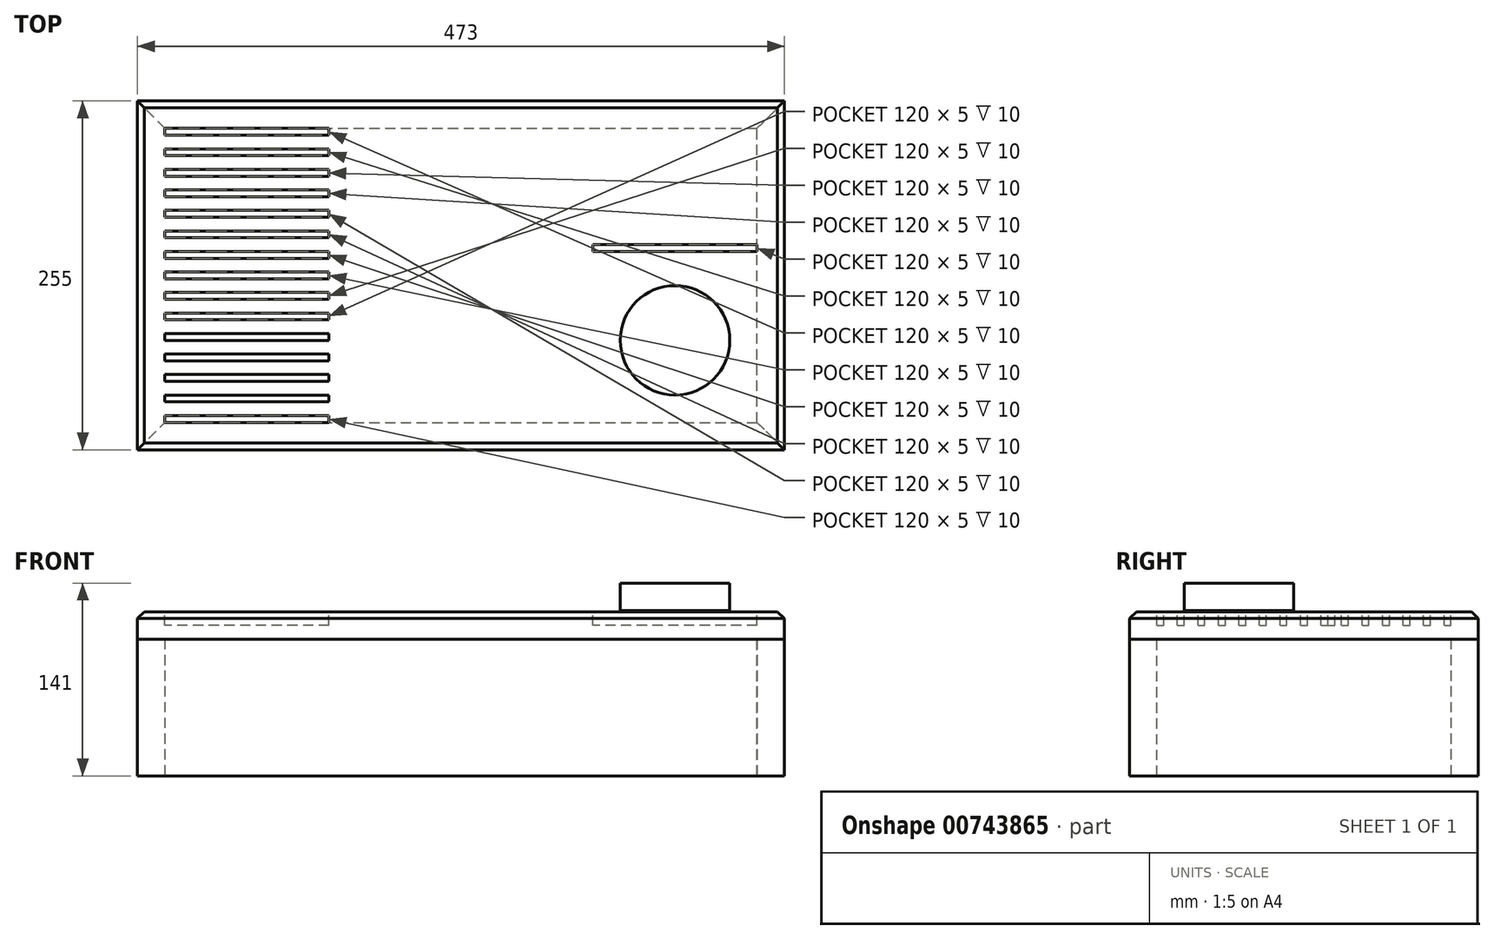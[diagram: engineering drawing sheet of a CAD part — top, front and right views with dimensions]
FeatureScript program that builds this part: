
annotation { "Feature Type Name" : "Feature", "Feature Type Description" : "" }
export const myFeature = defineFeature(function(context is Context, id is Id, definition is map)
    precondition{}
    {
        {
            var Q0;
            Q0=qCreatedBy(makeId("Top.planeOp"),FACE);
            var sketch = newSketch(context, id + "F0", { "sketchPlane" : qUnion([Q0])});
            skPoint(sketch, "E0.middle", {"position": v(0, 0) * mm});
            skLineSegment(sketch, "E1.bottom", {"start": v(-236.5, 127.5) * mm, "end": v(236.5, 127.5) * mm});
            skLineSegment(sketch, "E1.top", {"start": v(-236.5, 107.5) * mm, "end": v(236.5, 107.5) * mm});
            skLineSegment(sketch, "E1.left", {"start": v(-236.5, 127.5) * mm, "end": v(-236.5, 107.5) * mm});
            skLineSegment(sketch, "E1.right", {"start": v(236.5, 127.5) * mm, "end": v(236.5, 107.5) * mm});
            skLineSegment(sketch, "E2.bottom", {"start": v(-236.5, -127.5) * mm, "end": v(236.5, -127.5) * mm});
            skLineSegment(sketch, "E2.top", {"start": v(-236.5, -107.5) * mm, "end": v(236.5, -107.5) * mm});
            skLineSegment(sketch, "E2.left", {"start": v(-236.5, -127.5) * mm, "end": v(-236.5, -107.5) * mm});
            skLineSegment(sketch, "E2.right", {"start": v(236.5, -127.5) * mm, "end": v(236.5, -107.5) * mm});
            skSolve(sketch);
        }
        {
            var Q0;
            Q0=qCreatedBy(makeId("Top.planeOp"),FACE);
            var sketch = newSketch(context, id + "F1", { "sketchPlane" : qUnion([Q0])});
            skLineSegment(sketch, "E3.bottom", {"start": v(-216.5, -127.5) * mm, "end": v(-236.5, -127.5) * mm});
            skLineSegment(sketch, "E3.top", {"start": v(-216.5, 127.5) * mm, "end": v(-236.5, 127.5) * mm});
            skLineSegment(sketch, "E3.left", {"start": v(-216.5, -127.5) * mm, "end": v(-216.5, 127.5) * mm});
            skLineSegment(sketch, "E3.right", {"start": v(-236.5, -127.5) * mm, "end": v(-236.5, 127.5) * mm});
            skPoint(sketch, "E3.middle", {"position": v(0, 0) * mm});
            skLineSegment(sketch, "E4.bottom", {"start": v(236.5, -127.5) * mm, "end": v(216.5, -127.5) * mm});
            skLineSegment(sketch, "E4.top", {"start": v(236.5, 127.5) * mm, "end": v(216.5, 127.5) * mm});
            skLineSegment(sketch, "E4.left", {"start": v(236.5, -127.5) * mm, "end": v(236.5, 127.5) * mm});
            skLineSegment(sketch, "E4.right", {"start": v(216.5, -127.5) * mm, "end": v(216.5, 127.5) * mm});
            skSolve(sketch);
        }
        {
            var Q0;
            Q0=makeQuery(id+"F1.imprint","IMPRINT",FACE,{"disambiguationData":[TD([[makeQuery(id+"F1.imprint","IMPRINT",EDGE,{"derivedFrom":sQuery(id+"F1.wireOp",EDGE,"E3.bottom")}),-1.0]])]});
            extrude(context, id + "F2", {"entities" : qUnion([Q0]), "depth" : 100 * mm, "offsetDistance" : 25 * mm});
        }
        {
            var Q0;
            Q0=makeQuery(id+"F1.imprint","IMPRINT",FACE,{"disambiguationData":[TD([[makeQuery(id+"F1.imprint","IMPRINT",EDGE,{"derivedFrom":sQuery(id+"F1.wireOp",EDGE,"E4.bottom")}),-1.0]])]});
            extrude(context, id + "F3", {"entities" : qUnion([Q0]), "depth" : 100 * mm, "offsetDistance" : 25 * mm});
        }
        {
            var Q0;
            Q0=makeQuery(id+"F0.imprint","IMPRINT",FACE,{"disambiguationData":[TD([[makeQuery(id+"F0.imprint","IMPRINT",EDGE,{"derivedFrom":sQuery(id+"F0.wireOp",EDGE,"E2.bottom")}),1.0]])]});
            extrude(context, id + "F4", {"entities" : qUnion([Q0]), "depth" : 100 * mm, "offsetDistance" : 25 * mm});
        }
        {
            var Q0;
            Q0=makeQuery(id+"F0.imprint","IMPRINT",FACE,{"disambiguationData":[TD([[makeQuery(id+"F0.imprint","IMPRINT",EDGE,{"derivedFrom":sQuery(id+"F0.wireOp",EDGE,"E1.bottom")}),-1.0]])]});
            extrude(context, id + "F5", {"entities" : qUnion([Q0]), "depth" : 100 * mm, "offsetDistance" : 25 * mm});
        }
        {
            var Q0;
            Q0=makeQuery(id+"F2.opExtrude","SWEPT_EDGE",EDGE,{"disambiguationData":[OSD([sQuery(id+"F1.wireOp",EDGE,"E3.bottom"),sQuery(id+"F1.wireOp",EDGE,"E3.left")])]});
            var Q1;
            Q1=makeQuery(id+"F2.opExtrude","SWEPT_EDGE",EDGE,{"disambiguationData":[OSD([sQuery(id+"F1.wireOp",EDGE,"E3.top"),sQuery(id+"F1.wireOp",EDGE,"E3.left")])]});
            chamfer(context, id + "F6", {"entities" : qUnion([Q0, Q1]), "width" : 20 * mm, "tangentPropagation" : true});
        }
        {
            var Q0;
            Q0=makeQuery(id+"F3.opExtrude","SWEPT_EDGE",EDGE,{"disambiguationData":[OSD([sQuery(id+"F1.wireOp",EDGE,"E4.bottom"),sQuery(id+"F1.wireOp",EDGE,"E4.right")])]});
            var Q1;
            Q1=makeQuery(id+"F3.opExtrude","SWEPT_EDGE",EDGE,{"disambiguationData":[OSD([sQuery(id+"F1.wireOp",EDGE,"E4.top"),sQuery(id+"F1.wireOp",EDGE,"E4.right")])]});
            chamfer(context, id + "F7", {"entities" : qUnion([Q0, Q1]), "width" : 20 * mm, "tangentPropagation" : true});
        }
        {
            var Q0;
            Q0=makeQuery(id+"F4.opExtrude","SWEPT_EDGE",EDGE,{"disambiguationData":[OSD([sQuery(id+"F0.wireOp",EDGE,"E2.top"),sQuery(id+"F0.wireOp",EDGE,"E2.right")])]});
            var Q1;
            Q1=makeQuery(id+"F4.opExtrude","SWEPT_EDGE",EDGE,{"disambiguationData":[OSD([sQuery(id+"F0.wireOp",EDGE,"E2.top"),sQuery(id+"F0.wireOp",EDGE,"E2.left")])]});
            chamfer(context, id + "F8", {"entities" : qUnion([Q0, Q1]), "width" : 20 * mm, "tangentPropagation" : true});
        }
        {
            var Q0;
            Q0=makeQuery(id+"F5.opExtrude","SWEPT_EDGE",EDGE,{"disambiguationData":[OSD([sQuery(id+"F0.wireOp",EDGE,"E1.top"),sQuery(id+"F0.wireOp",EDGE,"E1.left")])]});
            var Q1;
            Q1=makeQuery(id+"F5.opExtrude","SWEPT_EDGE",EDGE,{"disambiguationData":[OSD([sQuery(id+"F0.wireOp",EDGE,"E1.top"),sQuery(id+"F0.wireOp",EDGE,"E1.right")])]});
            chamfer(context, id + "F9", {"entities" : qUnion([Q0, Q1]), "width" : 20 * mm, "tangentPropagation" : true});
        }
        {
            var Q0;
            Q0=qCreatedBy(makeId("Top.planeOp"),FACE);
            var sketch = newSketch(context, id + "F10", { "sketchPlane" : qUnion([Q0])});
            skLineSegment(sketch, "E5.bottom", {"start": v(236.5, -127.5) * mm, "end": v(-236.5, -127.5) * mm});
            skLineSegment(sketch, "E5.top", {"start": v(236.5, 127.5) * mm, "end": v(-236.5, 127.5) * mm});
            skLineSegment(sketch, "E5.left", {"start": v(236.5, -127.5) * mm, "end": v(236.5, 127.5) * mm});
            skLineSegment(sketch, "E5.right", {"start": v(-236.5, -127.5) * mm, "end": v(-236.5, 127.5) * mm});
            skPoint(sketch, "E5.middle", {"position": v(0, 0) * mm});
            skSolve(sketch);
        }
        {
            var Q0;
            Q0 = qSketchRegion(id + "F10", true);
            extrude(context, id + "F11", {"entities" : qUnion([Q0]), "depth" : 20 * mm, "offsetDistance" : 25 * mm});
        }
        {
            var Q0;
            Q0=makeQuery(id+"F11.opExtrude","SWEPT_BODY",BODY,{"disambiguationData":[OSD([sQuery(id+"F10.wireOp",EDGE,"E5.bottom"),sQuery(id+"F10.wireOp",EDGE,"E5.top"),sQuery(id+"F10.wireOp",EDGE,"E5.left"),sQuery(id+"F10.wireOp",EDGE,"E5.right")])]});
            transform(context, id + "F12", {"entities" : qUnion([Q0]), "transformType" : TransformType.TRANSLATION_3D, "dx" : 0 * mm, "dy" : 0 * mm, "dz" : 100 * mm, "makeCopy" : false});
        }
        {
            var Q0;
            Q0=makeQuery(id+"F11.opExtrude","CAP_FACE",FACE,{"disambiguationData":[OSD([sQuery(id+"F10.wireOp",EDGE,"E5.bottom"),sQuery(id+"F10.wireOp",EDGE,"E5.top"),sQuery(id+"F10.wireOp",EDGE,"E5.left"),sQuery(id+"F10.wireOp",EDGE,"E5.right")])],"isStart":false});
            chamfer(context, id + "F13", {"entities" : qUnion([Q0]), "width" : 5 * mm, "tangentPropagation" : true});
        }
        {
            var Q0;
            Q0=qCreatedBy(makeId("Top.planeOp"),FACE);
            var sketch = newSketch(context, id + "F14", { "sketchPlane" : qUnion([Q0])});
            skLineSegment(sketch, "E6.bottom", {"start": v(-96.5, 102.5) * mm, "end": v(-216.5, 102.5) * mm});
            skLineSegment(sketch, "E6.top", {"start": v(-96.5, 107.5) * mm, "end": v(-216.5, 107.5) * mm});
            skLineSegment(sketch, "E6.left", {"start": v(-96.5, 102.5) * mm, "end": v(-96.5, 107.5) * mm});
            skLineSegment(sketch, "E6.right", {"start": v(-216.5, 102.5) * mm, "end": v(-216.5, 107.5) * mm});
            skPoint(sketch, "E6.middle", {"position": v(0, -2.5) * mm});
            skLineSegment(sketch, "E7.bottom", {"start": v(-96.5, 87.5) * mm, "end": v(-216.5, 87.5) * mm});
            skLineSegment(sketch, "E7.top", {"start": v(-96.5, 92.5) * mm, "end": v(-216.5, 92.5) * mm});
            skLineSegment(sketch, "E7.left", {"start": v(-96.5, 87.5) * mm, "end": v(-96.5, 92.5) * mm});
            skLineSegment(sketch, "E7.right", {"start": v(-216.5, 87.5) * mm, "end": v(-216.5, 92.5) * mm});
            skPoint(sketch, "E7.middle", {"position": v(0, -15) * mm});
            skLineSegment(sketch, "E8.bottom", {"start": v(-96.5, 72.5) * mm, "end": v(-216.5, 72.5) * mm});
            skLineSegment(sketch, "E8.top", {"start": v(-96.5, 77.5) * mm, "end": v(-216.5, 77.5) * mm});
            skLineSegment(sketch, "E8.left", {"start": v(-96.5, 72.5) * mm, "end": v(-96.5, 77.5) * mm});
            skLineSegment(sketch, "E8.right", {"start": v(-216.5, 72.5) * mm, "end": v(-216.5, 77.5) * mm});
            skPoint(sketch, "E8.middle", {"position": v(0, -30.25) * mm});
            skLineSegment(sketch, "E9.bottom", {"start": v(-96.5, 57.5) * mm, "end": v(-216.5, 57.5) * mm});
            skLineSegment(sketch, "E9.top", {"start": v(-96.5, 62.5) * mm, "end": v(-216.5, 62.5) * mm});
            skLineSegment(sketch, "E9.left", {"start": v(-96.5, 57.5) * mm, "end": v(-96.5, 62.5) * mm});
            skLineSegment(sketch, "E9.right", {"start": v(-216.5, 57.5) * mm, "end": v(-216.5, 62.5) * mm});
            skPoint(sketch, "E9.middle", {"position": v(0, -42.75) * mm});
            skLineSegment(sketch, "E10.bottom", {"start": v(-96.5, 42.5) * mm, "end": v(-216.5, 42.5) * mm});
            skLineSegment(sketch, "E10.top", {"start": v(-96.5, 47.5) * mm, "end": v(-216.5, 47.5) * mm});
            skLineSegment(sketch, "E10.left", {"start": v(-96.5, 42.5) * mm, "end": v(-96.5, 47.5) * mm});
            skLineSegment(sketch, "E10.right", {"start": v(-216.5, 42.5) * mm, "end": v(-216.5, 47.5) * mm});
            skPoint(sketch, "E10.middle", {"position": v(0, -59.75) * mm});
            skLineSegment(sketch, "E11.bottom", {"start": v(-96.5, 27.5) * mm, "end": v(-216.5, 27.5) * mm});
            skLineSegment(sketch, "E11.top", {"start": v(-96.5, 32.5) * mm, "end": v(-216.5, 32.5) * mm});
            skLineSegment(sketch, "E11.left", {"start": v(-96.5, 27.5) * mm, "end": v(-96.5, 32.5) * mm});
            skLineSegment(sketch, "E11.right", {"start": v(-216.5, 27.5) * mm, "end": v(-216.5, 32.5) * mm});
            skPoint(sketch, "E11.middle", {"position": v(0, -72.25) * mm});
            skLineSegment(sketch, "E12.bottom", {"start": v(-96.5, 12.5) * mm, "end": v(-216.5, 12.5) * mm});
            skLineSegment(sketch, "E12.top", {"start": v(-96.5, 17.5) * mm, "end": v(-216.5, 17.5) * mm});
            skLineSegment(sketch, "E12.left", {"start": v(-96.5, 12.5) * mm, "end": v(-96.5, 17.5) * mm});
            skLineSegment(sketch, "E12.right", {"start": v(-216.5, 12.5) * mm, "end": v(-216.5, 17.5) * mm});
            skPoint(sketch, "E12.middle", {"position": v(0, -87.5) * mm});
            skLineSegment(sketch, "E13.bottom", {"start": v(-96.5, -2.5) * mm, "end": v(-216.5, -2.5) * mm});
            skLineSegment(sketch, "E13.top", {"start": v(-96.5, 2.5) * mm, "end": v(-216.5, 2.5) * mm});
            skLineSegment(sketch, "E13.left", {"start": v(-96.5, -2.5) * mm, "end": v(-96.5, 2.5) * mm});
            skLineSegment(sketch, "E13.right", {"start": v(-216.5, -2.5) * mm, "end": v(-216.5, 2.5) * mm});
            skPoint(sketch, "E13.middle", {"position": v(0, -100) * mm});
            skLineSegment(sketch, "E14.bottom", {"start": v(-96.5, -17.5) * mm, "end": v(-216.5, -17.5) * mm});
            skLineSegment(sketch, "E14.top", {"start": v(-96.5, -12.5) * mm, "end": v(-216.5, -12.5) * mm});
            skLineSegment(sketch, "E14.left", {"start": v(-96.5, -17.5) * mm, "end": v(-96.5, -12.5) * mm});
            skLineSegment(sketch, "E14.right", {"start": v(-216.5, -17.5) * mm, "end": v(-216.5, -12.5) * mm});
            skPoint(sketch, "E14.middle", {"position": v(0, -132.01) * mm});
            skLineSegment(sketch, "E15.bottom", {"start": v(-96.5, -32.5) * mm, "end": v(-216.5, -32.5) * mm});
            skLineSegment(sketch, "E15.top", {"start": v(-96.5, -27.5) * mm, "end": v(-216.5, -27.5) * mm});
            skLineSegment(sketch, "E15.left", {"start": v(-96.5, -32.5) * mm, "end": v(-96.5, -27.5) * mm});
            skLineSegment(sketch, "E15.right", {"start": v(-216.5, -32.5) * mm, "end": v(-216.5, -27.5) * mm});
            skPoint(sketch, "E15.middle", {"position": v(0, -142.01) * mm});
            skLineSegment(sketch, "E16.bottom", {"start": v(-96.5, -47.5) * mm, "end": v(-216.5, -47.5) * mm});
            skLineSegment(sketch, "E16.top", {"start": v(-96.5, -42.5) * mm, "end": v(-216.5, -42.5) * mm});
            skLineSegment(sketch, "E16.left", {"start": v(-96.5, -47.5) * mm, "end": v(-96.5, -42.5) * mm});
            skLineSegment(sketch, "E16.right", {"start": v(-216.5, -47.5) * mm, "end": v(-216.5, -42.5) * mm});
            skPoint(sketch, "E16.middle", {"position": v(0, -157.26) * mm});
            skLineSegment(sketch, "E17.bottom", {"start": v(-96.5, -62.5) * mm, "end": v(-216.5, -62.5) * mm});
            skLineSegment(sketch, "E17.top", {"start": v(-96.5, -57.5) * mm, "end": v(-216.5, -57.5) * mm});
            skLineSegment(sketch, "E17.left", {"start": v(-96.5, -62.5) * mm, "end": v(-96.5, -57.5) * mm});
            skLineSegment(sketch, "E17.right", {"start": v(-216.5, -62.5) * mm, "end": v(-216.5, -57.5) * mm});
            skPoint(sketch, "E17.middle", {"position": v(0, -169.76) * mm});
            skLineSegment(sketch, "E18.bottom", {"start": v(-96.5, -77.5) * mm, "end": v(-216.5, -77.5) * mm});
            skLineSegment(sketch, "E18.top", {"start": v(-96.5, -72.5) * mm, "end": v(-216.5, -72.5) * mm});
            skLineSegment(sketch, "E18.left", {"start": v(-96.5, -77.5) * mm, "end": v(-96.5, -72.5) * mm});
            skLineSegment(sketch, "E18.right", {"start": v(-216.5, -77.5) * mm, "end": v(-216.5, -72.5) * mm});
            skPoint(sketch, "E18.middle", {"position": v(0, -186.77) * mm});
            skLineSegment(sketch, "E19.bottom", {"start": v(-96.5, -92.5) * mm, "end": v(-216.5, -92.5) * mm});
            skLineSegment(sketch, "E19.top", {"start": v(-96.5, -87.5) * mm, "end": v(-216.5, -87.5) * mm});
            skLineSegment(sketch, "E19.left", {"start": v(-96.5, -92.5) * mm, "end": v(-96.5, -87.5) * mm});
            skLineSegment(sketch, "E19.right", {"start": v(-216.5, -92.5) * mm, "end": v(-216.5, -87.5) * mm});
            skPoint(sketch, "E19.middle", {"position": v(0, -199.27) * mm});
            skLineSegment(sketch, "E20.bottom", {"start": v(-96.5, -107.5) * mm, "end": v(-216.5, -107.5) * mm});
            skLineSegment(sketch, "E20.top", {"start": v(-96.5, -102.5) * mm, "end": v(-216.5, -102.5) * mm});
            skLineSegment(sketch, "E20.left", {"start": v(-96.5, -107.5) * mm, "end": v(-96.5, -102.5) * mm});
            skLineSegment(sketch, "E20.right", {"start": v(-216.5, -107.5) * mm, "end": v(-216.5, -102.5) * mm});
            skPoint(sketch, "E20.middle", {"position": v(0, -214.51) * mm});
            skPoint(sketch, "E21.middle", {"position": v(0, -227.01) * mm});
            skLineSegment(sketch, "E22.bottom", {"start": v(43.5, -2.5) * mm, "end": v(-76.5, -2.5) * mm});
            skLineSegment(sketch, "E22.top", {"start": v(43.5, 2.5) * mm, "end": v(-76.5, 2.5) * mm});
            skLineSegment(sketch, "E22.left", {"start": v(43.5, -2.5) * mm, "end": v(43.5, 2.5) * mm});
            skLineSegment(sketch, "E22.right", {"start": v(-76.5, -2.5) * mm, "end": v(-76.5, 2.5) * mm});
            skSolve(sketch);
        }
        {
            var Q0;
            Q0 = qSketchRegion(id + "F14", true);
            extrude(context, id + "F15", {"entities" : qUnion([Q0]), "oppositeDirection" : true, "depth" : 10 * mm, "offsetDistance" : 25 * mm});
        }
        {
            var Q0;
            Q0=makeQuery(id+"F15.opExtrude","SWEPT_BODY",BODY,{"disambiguationData":[OSD([sQuery(id+"F14.wireOp",EDGE,"E20.bottom"),sQuery(id+"F14.wireOp",EDGE,"E20.top"),sQuery(id+"F14.wireOp",EDGE,"E20.left"),sQuery(id+"F14.wireOp",EDGE,"E20.right")])]});
            var Q1;
            Q1=makeQuery(id+"F15.opExtrude","SWEPT_BODY",BODY,{"disambiguationData":[OSD([sQuery(id+"F14.wireOp",EDGE,"E19.bottom"),sQuery(id+"F14.wireOp",EDGE,"E19.top"),sQuery(id+"F14.wireOp",EDGE,"E19.left"),sQuery(id+"F14.wireOp",EDGE,"E19.right")])]});
            var Q2;
            Q2=makeQuery(id+"F15.opExtrude","SWEPT_BODY",BODY,{"disambiguationData":[OSD([sQuery(id+"F14.wireOp",EDGE,"E18.bottom"),sQuery(id+"F14.wireOp",EDGE,"E18.top"),sQuery(id+"F14.wireOp",EDGE,"E18.left"),sQuery(id+"F14.wireOp",EDGE,"E18.right")])]});
            var Q3;
            Q3=makeQuery(id+"F15.opExtrude","SWEPT_BODY",BODY,{"disambiguationData":[OSD([sQuery(id+"F14.wireOp",EDGE,"E17.bottom"),sQuery(id+"F14.wireOp",EDGE,"E17.top"),sQuery(id+"F14.wireOp",EDGE,"E17.left"),sQuery(id+"F14.wireOp",EDGE,"E17.right")])]});
            var Q4;
            Q4=makeQuery(id+"F15.opExtrude","SWEPT_BODY",BODY,{"disambiguationData":[OSD([sQuery(id+"F14.wireOp",EDGE,"E16.bottom"),sQuery(id+"F14.wireOp",EDGE,"E16.top"),sQuery(id+"F14.wireOp",EDGE,"E16.left"),sQuery(id+"F14.wireOp",EDGE,"E16.right")])]});
            var Q5;
            Q5=makeQuery(id+"F15.opExtrude","SWEPT_BODY",BODY,{"disambiguationData":[OSD([sQuery(id+"F14.wireOp",EDGE,"E15.bottom"),sQuery(id+"F14.wireOp",EDGE,"E15.top"),sQuery(id+"F14.wireOp",EDGE,"E15.left"),sQuery(id+"F14.wireOp",EDGE,"E15.right")])]});
            var Q6;
            Q6=makeQuery(id+"F15.opExtrude","SWEPT_BODY",BODY,{"disambiguationData":[OSD([sQuery(id+"F14.wireOp",EDGE,"E10.bottom"),sQuery(id+"F14.wireOp",EDGE,"E10.top"),sQuery(id+"F14.wireOp",EDGE,"E10.left"),sQuery(id+"F14.wireOp",EDGE,"E10.right")])]});
            var Q7;
            Q7=makeQuery(id+"F15.opExtrude","SWEPT_BODY",BODY,{"disambiguationData":[OSD([sQuery(id+"F14.wireOp",EDGE,"E11.bottom"),sQuery(id+"F14.wireOp",EDGE,"E11.top"),sQuery(id+"F14.wireOp",EDGE,"E11.left"),sQuery(id+"F14.wireOp",EDGE,"E11.right")])]});
            var Q8;
            Q8=makeQuery(id+"F15.opExtrude","SWEPT_BODY",BODY,{"disambiguationData":[OSD([sQuery(id+"F14.wireOp",EDGE,"E12.bottom"),sQuery(id+"F14.wireOp",EDGE,"E12.top"),sQuery(id+"F14.wireOp",EDGE,"E12.left"),sQuery(id+"F14.wireOp",EDGE,"E12.right")])]});
            var Q9;
            Q9=makeQuery(id+"F15.opExtrude","SWEPT_BODY",BODY,{"disambiguationData":[OSD([sQuery(id+"F14.wireOp",EDGE,"E13.bottom"),sQuery(id+"F14.wireOp",EDGE,"E13.top"),sQuery(id+"F14.wireOp",EDGE,"E13.left"),sQuery(id+"F14.wireOp",EDGE,"E13.right")])]});
            var Q10;
            Q10=makeQuery(id+"F15.opExtrude","SWEPT_BODY",BODY,{"disambiguationData":[OSD([sQuery(id+"F14.wireOp",EDGE,"E14.bottom"),sQuery(id+"F14.wireOp",EDGE,"E14.top"),sQuery(id+"F14.wireOp",EDGE,"E14.left"),sQuery(id+"F14.wireOp",EDGE,"E14.right")])]});
            var Q11;
            Q11=makeQuery(id+"F15.opExtrude","SWEPT_BODY",BODY,{"disambiguationData":[OSD([sQuery(id+"F14.wireOp",EDGE,"E6.bottom"),sQuery(id+"F14.wireOp",EDGE,"E6.top"),sQuery(id+"F14.wireOp",EDGE,"E6.left"),sQuery(id+"F14.wireOp",EDGE,"E6.right")])]});
            var Q12;
            Q12=makeQuery(id+"F15.opExtrude","SWEPT_BODY",BODY,{"disambiguationData":[OSD([sQuery(id+"F14.wireOp",EDGE,"E7.bottom"),sQuery(id+"F14.wireOp",EDGE,"E7.top"),sQuery(id+"F14.wireOp",EDGE,"E7.left"),sQuery(id+"F14.wireOp",EDGE,"E7.right")])]});
            var Q13;
            Q13=makeQuery(id+"F15.opExtrude","SWEPT_BODY",BODY,{"disambiguationData":[OSD([sQuery(id+"F14.wireOp",EDGE,"E8.bottom"),sQuery(id+"F14.wireOp",EDGE,"E8.top"),sQuery(id+"F14.wireOp",EDGE,"E8.left"),sQuery(id+"F14.wireOp",EDGE,"E8.right")])]});
            var Q14;
            Q14=makeQuery(id+"F15.opExtrude","SWEPT_BODY",BODY,{"disambiguationData":[OSD([sQuery(id+"F14.wireOp",EDGE,"E9.bottom"),sQuery(id+"F14.wireOp",EDGE,"E9.top"),sQuery(id+"F14.wireOp",EDGE,"E9.left"),sQuery(id+"F14.wireOp",EDGE,"E9.right")])]});
            var Q15;
            Q15=makeQuery(id+"F15.opExtrude","SWEPT_BODY",BODY,{"disambiguationData":[OSD([sQuery(id+"F14.wireOp",EDGE,"E22.bottom"),sQuery(id+"F14.wireOp",EDGE,"E22.top"),sQuery(id+"F14.wireOp",EDGE,"E22.left"),sQuery(id+"F14.wireOp",EDGE,"E22.right")])]});
            transform(context, id + "F16", {"entities" : qUnion([Q0, Q1, Q2, Q3, Q4, Q5, Q6, Q7, Q8, Q9, Q10, Q11, Q12, Q13, Q14, Q15]), "transformType" : TransformType.TRANSLATION_3D, "dx" : 0 * mm, "dy" : 0 * mm, "dz" : 120 * mm, "makeCopy" : false});
        }
        {
            var Q0;
            Q0=makeQuery(id+"F15.opExtrude","SWEPT_BODY",BODY,{"disambiguationData":[OSD([sQuery(id+"F14.wireOp",EDGE,"E22.bottom"),sQuery(id+"F14.wireOp",EDGE,"E22.top"),sQuery(id+"F14.wireOp",EDGE,"E22.left"),sQuery(id+"F14.wireOp",EDGE,"E22.right")])]});
            transform(context, id + "F17", {"entities" : qUnion([Q0]), "transformType" : TransformType.TRANSLATION_3D, "dx" : 173 * mm, "dy" : 20 * mm, "dz" : 0 * mm, "makeCopy" : false});
        }
        {
            var Q0;
            Q0=makeQuery(id+"F15.opExtrude","SWEPT_BODY",BODY,{"disambiguationData":[OSD([sQuery(id+"F14.wireOp",EDGE,"E20.bottom"),sQuery(id+"F14.wireOp",EDGE,"E20.top"),sQuery(id+"F14.wireOp",EDGE,"E20.left"),sQuery(id+"F14.wireOp",EDGE,"E20.right")])]});
            var Q1;
            Q1=makeQuery(id+"F15.opExtrude","SWEPT_BODY",BODY,{"disambiguationData":[OSD([sQuery(id+"F14.wireOp",EDGE,"E19.bottom"),sQuery(id+"F14.wireOp",EDGE,"E19.top"),sQuery(id+"F14.wireOp",EDGE,"E19.left"),sQuery(id+"F14.wireOp",EDGE,"E19.right")])]});
            var Q2;
            Q2=makeQuery(id+"F15.opExtrude","SWEPT_BODY",BODY,{"disambiguationData":[OSD([sQuery(id+"F14.wireOp",EDGE,"E18.bottom"),sQuery(id+"F14.wireOp",EDGE,"E18.top"),sQuery(id+"F14.wireOp",EDGE,"E18.left"),sQuery(id+"F14.wireOp",EDGE,"E18.right")])]});
            var Q3;
            Q3=makeQuery(id+"F15.opExtrude","SWEPT_BODY",BODY,{"disambiguationData":[OSD([sQuery(id+"F14.wireOp",EDGE,"E17.bottom"),sQuery(id+"F14.wireOp",EDGE,"E17.top"),sQuery(id+"F14.wireOp",EDGE,"E17.left"),sQuery(id+"F14.wireOp",EDGE,"E17.right")])]});
            var Q4;
            Q4=makeQuery(id+"F15.opExtrude","SWEPT_BODY",BODY,{"disambiguationData":[OSD([sQuery(id+"F14.wireOp",EDGE,"E16.bottom"),sQuery(id+"F14.wireOp",EDGE,"E16.top"),sQuery(id+"F14.wireOp",EDGE,"E16.left"),sQuery(id+"F14.wireOp",EDGE,"E16.right")])]});
            var Q5;
            Q5=makeQuery(id+"F15.opExtrude","SWEPT_BODY",BODY,{"disambiguationData":[OSD([sQuery(id+"F14.wireOp",EDGE,"E15.bottom"),sQuery(id+"F14.wireOp",EDGE,"E15.top"),sQuery(id+"F14.wireOp",EDGE,"E15.left"),sQuery(id+"F14.wireOp",EDGE,"E15.right")])]});
            var Q6;
            Q6=makeQuery(id+"F15.opExtrude","SWEPT_BODY",BODY,{"disambiguationData":[OSD([sQuery(id+"F14.wireOp",EDGE,"E14.bottom"),sQuery(id+"F14.wireOp",EDGE,"E14.top"),sQuery(id+"F14.wireOp",EDGE,"E14.left"),sQuery(id+"F14.wireOp",EDGE,"E14.right")])]});
            var Q7;
            Q7=makeQuery(id+"F15.opExtrude","SWEPT_BODY",BODY,{"disambiguationData":[OSD([sQuery(id+"F14.wireOp",EDGE,"E8.bottom"),sQuery(id+"F14.wireOp",EDGE,"E8.top"),sQuery(id+"F14.wireOp",EDGE,"E8.left"),sQuery(id+"F14.wireOp",EDGE,"E8.right")])]});
            var Q8;
            Q8=makeQuery(id+"F15.opExtrude","SWEPT_BODY",BODY,{"disambiguationData":[OSD([sQuery(id+"F14.wireOp",EDGE,"E9.bottom"),sQuery(id+"F14.wireOp",EDGE,"E9.top"),sQuery(id+"F14.wireOp",EDGE,"E9.left"),sQuery(id+"F14.wireOp",EDGE,"E9.right")])]});
            var Q9;
            Q9=makeQuery(id+"F15.opExtrude","SWEPT_BODY",BODY,{"disambiguationData":[OSD([sQuery(id+"F14.wireOp",EDGE,"E10.bottom"),sQuery(id+"F14.wireOp",EDGE,"E10.top"),sQuery(id+"F14.wireOp",EDGE,"E10.left"),sQuery(id+"F14.wireOp",EDGE,"E10.right")])]});
            var Q10;
            Q10=makeQuery(id+"F15.opExtrude","SWEPT_BODY",BODY,{"disambiguationData":[OSD([sQuery(id+"F14.wireOp",EDGE,"E11.bottom"),sQuery(id+"F14.wireOp",EDGE,"E11.top"),sQuery(id+"F14.wireOp",EDGE,"E11.left"),sQuery(id+"F14.wireOp",EDGE,"E11.right")])]});
            var Q11;
            Q11=makeQuery(id+"F15.opExtrude","SWEPT_BODY",BODY,{"disambiguationData":[OSD([sQuery(id+"F14.wireOp",EDGE,"E12.bottom"),sQuery(id+"F14.wireOp",EDGE,"E12.top"),sQuery(id+"F14.wireOp",EDGE,"E12.left"),sQuery(id+"F14.wireOp",EDGE,"E12.right")])]});
            var Q12;
            Q12=makeQuery(id+"F15.opExtrude","SWEPT_BODY",BODY,{"disambiguationData":[OSD([sQuery(id+"F14.wireOp",EDGE,"E13.bottom"),sQuery(id+"F14.wireOp",EDGE,"E13.top"),sQuery(id+"F14.wireOp",EDGE,"E13.left"),sQuery(id+"F14.wireOp",EDGE,"E13.right")])]});
            var Q13;
            Q13=makeQuery(id+"F15.opExtrude","SWEPT_BODY",BODY,{"disambiguationData":[OSD([sQuery(id+"F14.wireOp",EDGE,"E6.bottom"),sQuery(id+"F14.wireOp",EDGE,"E6.top"),sQuery(id+"F14.wireOp",EDGE,"E6.left"),sQuery(id+"F14.wireOp",EDGE,"E6.right")])]});
            var Q14;
            Q14=makeQuery(id+"F15.opExtrude","SWEPT_BODY",BODY,{"disambiguationData":[OSD([sQuery(id+"F14.wireOp",EDGE,"E7.bottom"),sQuery(id+"F14.wireOp",EDGE,"E7.top"),sQuery(id+"F14.wireOp",EDGE,"E7.left"),sQuery(id+"F14.wireOp",EDGE,"E7.right")])]});
            var Q15;
            Q15=makeQuery(id+"F15.opExtrude","SWEPT_BODY",BODY,{"disambiguationData":[OSD([sQuery(id+"F14.wireOp",EDGE,"E22.bottom"),sQuery(id+"F14.wireOp",EDGE,"E22.top"),sQuery(id+"F14.wireOp",EDGE,"E22.left"),sQuery(id+"F14.wireOp",EDGE,"E22.right")])]});
            var Q16;
            Q16=makeQuery(id+"F11.opExtrude","SWEPT_BODY",BODY,{"disambiguationData":[OSD([sQuery(id+"F10.wireOp",EDGE,"E5.bottom"),sQuery(id+"F10.wireOp",EDGE,"E5.top"),sQuery(id+"F10.wireOp",EDGE,"E5.left"),sQuery(id+"F10.wireOp",EDGE,"E5.right")])]});
            booleanBodies(context, id + "F18", {"operationType" : BooleanOperationType.SUBTRACTION, "tools" : qUnion([Q0, Q1, Q2, Q3, Q4, Q5, Q6, Q7, Q8, Q9, Q10, Q11, Q12, Q13, Q14, Q15]), "targets" : qUnion([Q16])});
        }
        {
            var Q0;
            Q0=qCreatedBy(makeId("Top.planeOp"),FACE);
            var sketch = newSketch(context, id + "F19", { "sketchPlane" : qUnion([Q0])});
            skCircle(sketch, "E23", {"center": v(156.5, -47.5) * mm, "radius": 40 * mm});
            skSolve(sketch);
        }
        {
            var Q0;
            Q0 = qSketchRegion(id + "F19", true);
            extrude(context, id + "F20", {"entities" : qUnion([Q0]), "depth" : 20 * mm, "offsetDistance" : 25 * mm});
        }
        {
            var Q0;
            Q0=makeQuery(id+"F20.opExtrude","SWEPT_BODY",BODY,{"disambiguationData":[OSD([sQuery(id+"F19.wireOp",EDGE,"E23")])]});
            transform(context, id + "F21", {"entities" : qUnion([Q0]), "transformType" : TransformType.TRANSLATION_3D, "dx" : 0 * mm, "dy" : 0 * mm, "dz" : 121 * mm, "makeCopy" : false});
        }
    });
